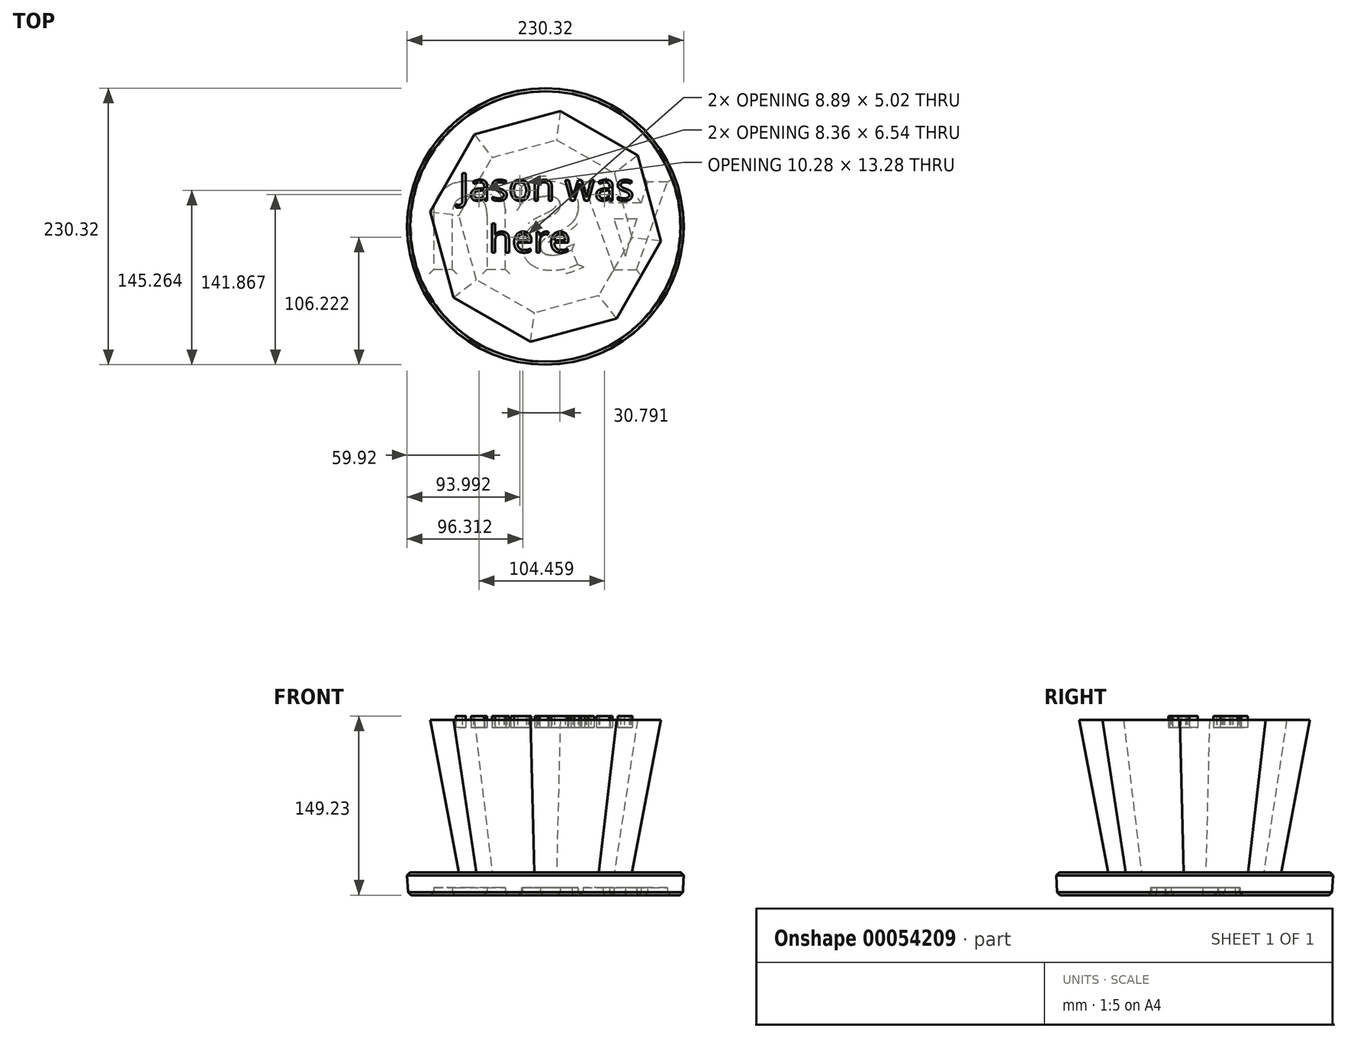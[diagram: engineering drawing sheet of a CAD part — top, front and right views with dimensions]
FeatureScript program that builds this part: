
annotation { "Feature Type Name" : "Feature", "Feature Type Description" : "" }
export const myFeature = defineFeature(function(context is Context, id is Id, definition is map)
    precondition{}
    {
        {
            var Q0;
            Q0=qCreatedBy(makeId("Top.planeOp"),FACE);
            var sketch = newSketch(context, id + "F0", { "sketchPlane" : qUnion([Q0])});
            skCircle(sketch, "E0", {"center": v(3.1, -0.22) * mm, "radius": 114.3 * mm});
            skSolve(sketch);
        }
        {
            var Q0;
            Q0=makeQuery(id+"F0.imprint","IMPRINT",FACE,{"disambiguationData":[TD([[makeQuery(id+"F0.imprint","IMPRINT",EDGE,{"derivedFrom":sQuery(id+"F0.wireOp",EDGE,"E0")}),1.0]])]});
            extrude(context, id + "F1", {"entities" : qUnion([Q0]), "depth" : 19.05 * mm, "hasDraft" : true, "draftAngle" : 3 * degree});
        }
        {
            var Q0;
            Q0=makeQuery(id+"F1.opExtrude","CAP_FACE",FACE,{"disambiguationData":[OSD([sQuery(id+"F0.wireOp",EDGE,"E0")])],"isStart":true});
            var sketch = newSketch(context, id + "F2", { "sketchPlane" : qUnion([Q0])});
            skText(sketch, "E1", { "text": "USA", "fontName": "OpenSans-Bold.ttf"});
            const initialGuessF2  = {"E1": [-0.0985, -0.0367, 1, 0, 0.07327]};
            skSetInitialGuess(sketch, initialGuessF2);
            skSolve(sketch);
        }
        {
            var Q0;
            Q0 = qSketchRegion(id + "F2", true);
            extrude(context, id + "F3", {"entities" : qUnion([Q0]), "operationType" : NewBodyOperationType.REMOVE, "oppositeDirection" : true, "depth" : 6.35 * mm});
        }
        {
            var Q0;
            Q0=makeQuery(id+"F1.opExtrude","CAP_EDGE",EDGE,{"disambiguationData":[OSD([sQuery(id+"F0.wireOp",EDGE,"E0")])],"isStart":true});
            var Q1;
            Q1=makeQuery(id+"F1.opExtrude","CAP_EDGE",EDGE,{"disambiguationData":[OSD([sQuery(id+"F0.wireOp",EDGE,"E0")])],"isStart":false});
            chamfer(context, id + "F4", {"entities" : qUnion([Q0, Q1]), "width" : 2.54 * mm});
        }
        {
            var Q0;
            Q0=makeQuery(id+"F3.boolean.opBoolean","COPY",EDGE,{"derivedFrom":makeQuery(id+"F3.opExtrude","CAP_EDGE",EDGE,{"disambiguationData":[OSD([sQuery(id+"F2.wireOp",EDGE,"E1.sketch_text.stroke-8")])],"isStart":true})});
            var Q1;
            Q1=makeQuery(id+"F3.boolean.opBoolean","COPY",EDGE,{"derivedFrom":makeQuery(id+"F3.opExtrude","CAP_EDGE",EDGE,{"disambiguationData":[OSD([sQuery(id+"F2.wireOp",EDGE,"E1.sketch_text.stroke-9")])],"isStart":true})});
            var Q2;
            Q2=makeQuery(id+"F3.boolean.opBoolean","COPY",EDGE,{"derivedFrom":makeQuery(id+"F3.opExtrude","CAP_EDGE",EDGE,{"disambiguationData":[OSD([sQuery(id+"F2.wireOp",EDGE,"E1.sketch_text.stroke-0")])],"isStart":true})});
            var Q3;
            Q3=makeQuery(id+"F3.boolean.opBoolean","COPY",EDGE,{"derivedFrom":makeQuery(id+"F3.opExtrude","CAP_EDGE",EDGE,{"disambiguationData":[OSD([sQuery(id+"F2.wireOp",EDGE,"E1.sketch_text.stroke-2")])],"isStart":true})});
            var Q4;
            Q4=makeQuery(id+"F3.boolean.opBoolean","COPY",EDGE,{"derivedFrom":makeQuery(id+"F3.opExtrude","CAP_EDGE",EDGE,{"disambiguationData":[OSD([sQuery(id+"F2.wireOp",EDGE,"E1.sketch_text.stroke-1")])],"isStart":true})});
            var Q5;
            Q5=makeQuery(id+"F3.boolean.opBoolean","COPY",EDGE,{"derivedFrom":makeQuery(id+"F3.opExtrude","CAP_EDGE",EDGE,{"disambiguationData":[OSD([sQuery(id+"F2.wireOp",EDGE,"E1.sketch_text.stroke-42")])],"isStart":true})});
            var Q6;
            Q6=makeQuery(id+"F3.boolean.opBoolean","COPY",EDGE,{"derivedFrom":makeQuery(id+"F3.opExtrude","CAP_EDGE",EDGE,{"disambiguationData":[OSD([sQuery(id+"F2.wireOp",EDGE,"E1.sketch_text.stroke-41")])],"isStart":true})});
            var Q7;
            Q7=makeQuery(id+"F3.boolean.opBoolean","COPY",EDGE,{"derivedFrom":makeQuery(id+"F3.opExtrude","CAP_EDGE",EDGE,{"disambiguationData":[OSD([sQuery(id+"F2.wireOp",EDGE,"E1.sketch_text.stroke-37")])],"isStart":true})});
            var Q8;
            Q8=makeQuery(id+"F3.boolean.opBoolean","COPY",EDGE,{"derivedFrom":makeQuery(id+"F3.opExtrude","CAP_EDGE",EDGE,{"disambiguationData":[OSD([sQuery(id+"F2.wireOp",EDGE,"E1.sketch_text.stroke-31")])],"isStart":true})});
            var Q9;
            Q9=makeQuery(id+"F3.boolean.opBoolean","COPY",EDGE,{"derivedFrom":makeQuery(id+"F3.opExtrude","CAP_EDGE",EDGE,{"disambiguationData":[OSD([sQuery(id+"F2.wireOp",EDGE,"E1.sketch_text.stroke-29")])],"isStart":true})});
            var Q10;
            Q10=makeQuery(id+"F3.boolean.opBoolean","COPY",EDGE,{"derivedFrom":makeQuery(id+"F3.opExtrude","CAP_EDGE",EDGE,{"disambiguationData":[OSD([sQuery(id+"F2.wireOp",EDGE,"E1.sketch_text.stroke-26")])],"isStart":true})});
            var Q11;
            Q11=makeQuery(id+"F3.boolean.opBoolean","COPY",EDGE,{"derivedFrom":makeQuery(id+"F3.opExtrude","CAP_EDGE",EDGE,{"disambiguationData":[OSD([sQuery(id+"F2.wireOp",EDGE,"E1.sketch_text.stroke-22")])],"isStart":true})});
            var Q12;
            Q12=makeQuery(id+"F3.boolean.opBoolean","COPY",EDGE,{"derivedFrom":makeQuery(id+"F3.opExtrude","CAP_EDGE",EDGE,{"disambiguationData":[OSD([sQuery(id+"F2.wireOp",EDGE,"E1.sketch_text.stroke-18")])],"isStart":true})});
            var Q13;
            Q13=makeQuery(id+"F3.boolean.opBoolean","COPY",EDGE,{"derivedFrom":makeQuery(id+"F3.opExtrude","CAP_EDGE",EDGE,{"disambiguationData":[OSD([sQuery(id+"F2.wireOp",EDGE,"E1.sketch_text.stroke-20")])],"isStart":true})});
            var Q14;
            Q14=makeQuery(id+"F3.boolean.opBoolean","COPY",EDGE,{"derivedFrom":makeQuery(id+"F3.opExtrude","CAP_EDGE",EDGE,{"disambiguationData":[OSD([sQuery(id+"F2.wireOp",EDGE,"E1.sketch_text.stroke-33")])],"isStart":true})});
            var Q15;
            Q15=makeQuery(id+"F3.boolean.opBoolean","COPY",EDGE,{"derivedFrom":makeQuery(id+"F3.opExtrude","CAP_EDGE",EDGE,{"disambiguationData":[OSD([sQuery(id+"F2.wireOp",EDGE,"E1.sketch_text.stroke-22")])],"isStart":true})});
            var Q16;
            Q16=makeQuery(id+"F3.boolean.opBoolean","COPY",EDGE,{"derivedFrom":makeQuery(id+"F3.opExtrude","CAP_EDGE",EDGE,{"disambiguationData":[OSD([sQuery(id+"F2.wireOp",EDGE,"E1.sketch_text.stroke-47")])],"isStart":true})});
            var Q17;
            Q17=makeQuery(id+"F3.boolean.opBoolean","COPY",EDGE,{"derivedFrom":makeQuery(id+"F3.opExtrude","CAP_EDGE",EDGE,{"disambiguationData":[OSD([sQuery(id+"F2.wireOp",EDGE,"E1.sketch_text.stroke-48")])],"isStart":true})});
            var Q18;
            Q18=makeQuery(id+"F3.boolean.opBoolean","COPY",EDGE,{"derivedFrom":makeQuery(id+"F3.opExtrude","CAP_EDGE",EDGE,{"disambiguationData":[OSD([sQuery(id+"F2.wireOp",EDGE,"E1.sketch_text.stroke-49")])],"isStart":true})});
            var Q19;
            Q19=makeQuery(id+"F3.boolean.opBoolean","COPY",EDGE,{"derivedFrom":makeQuery(id+"F3.opExtrude","CAP_EDGE",EDGE,{"disambiguationData":[OSD([sQuery(id+"F2.wireOp",EDGE,"E1.sketch_text.stroke-53")])],"isStart":true})});
            var Q20;
            Q20=makeQuery(id+"F3.boolean.opBoolean","COPY",EDGE,{"derivedFrom":makeQuery(id+"F3.opExtrude","CAP_EDGE",EDGE,{"disambiguationData":[OSD([sQuery(id+"F2.wireOp",EDGE,"E1.sketch_text.stroke-51")])],"isStart":true})});
            var Q21;
            Q21=makeQuery(id+"F3.boolean.opBoolean","COPY",EDGE,{"derivedFrom":makeQuery(id+"F3.opExtrude","CAP_EDGE",EDGE,{"disambiguationData":[OSD([sQuery(id+"F2.wireOp",EDGE,"E1.sketch_text.stroke-54")])],"isStart":true})});
            var Q22;
            Q22=makeQuery(id+"F3.boolean.opBoolean","COPY",EDGE,{"derivedFrom":makeQuery(id+"F3.opExtrude","CAP_EDGE",EDGE,{"disambiguationData":[OSD([sQuery(id+"F2.wireOp",EDGE,"E1.sketch_text.stroke-44")])],"isStart":true})});
            var Q23;
            Q23=makeQuery(id+"F3.boolean.opBoolean","COPY",EDGE,{"derivedFrom":makeQuery(id+"F3.opExtrude","CAP_EDGE",EDGE,{"disambiguationData":[OSD([sQuery(id+"F2.wireOp",EDGE,"E1.sketch_text.stroke-45")])],"isStart":true})});
            var Q24;
            Q24=makeQuery(id+"F3.boolean.opBoolean","COPY",EDGE,{"derivedFrom":makeQuery(id+"F3.opExtrude","CAP_EDGE",EDGE,{"disambiguationData":[OSD([sQuery(id+"F2.wireOp",EDGE,"E1.sketch_text.stroke-46")])],"isStart":true})});
            var Q25;
            Q25=makeQuery(id+"F3.boolean.opBoolean","COPY",EDGE,{"derivedFrom":makeQuery(id+"F3.opExtrude","CAP_EDGE",EDGE,{"disambiguationData":[OSD([sQuery(id+"F2.wireOp",EDGE,"E1.sketch_text.stroke-43")])],"isStart":true})});
            var Q26;
            Q26=makeQuery(id+"F3.boolean.opBoolean","COPY",EDGE,{"derivedFrom":makeQuery(id+"F3.opExtrude","CAP_EDGE",EDGE,{"disambiguationData":[OSD([sQuery(id+"F2.wireOp",EDGE,"E1.sketch_text.stroke-50")])],"isStart":true})});
            var Q27;
            Q27=makeQuery(id+"F3.boolean.opBoolean","COPY",EDGE,{"derivedFrom":makeQuery(id+"F3.opExtrude","CAP_EDGE",EDGE,{"disambiguationData":[OSD([sQuery(id+"F2.wireOp",EDGE,"E1.sketch_text.stroke-7")])],"isStart":true})});
            var Q28;
            Q28=makeQuery(id+"F3.boolean.opBoolean","COPY",EDGE,{"derivedFrom":makeQuery(id+"F3.opExtrude","CAP_EDGE",EDGE,{"disambiguationData":[OSD([sQuery(id+"F2.wireOp",EDGE,"E1.sketch_text.stroke-14")])],"isStart":true})});
            fillet(context, id + "F5", {"entities" : qUnion([Q0, Q1, Q2, Q3, Q4, Q5, Q6, Q7, Q8, Q9, Q10, Q11, Q12, Q13, Q14, Q15, Q16, Q17, Q18, Q19, Q20, Q21, Q22, Q23, Q24, Q25, Q26, Q27, Q28]), "radius" : 3.8 * mm, "tangentPropagation" : true, "allowEdgeOverflow" : false});
        }
        {
            var Q0;
            Q0=makeQuery(id+"F1.opExtrude","CAP_FACE",FACE,{"disambiguationData":[OSD([sQuery(id+"F0.wireOp",EDGE,"E0")])],"isStart":false});
            var sketch = newSketch(context, id + "F6", { "sketchPlane" : qUnion([Q0])});
            skCircle(sketch, "E2.cCircle", {"center": v(3.1, -0.22) * mm, "radius": 67.1 * mm, "construction": true});
            skLineSegment(sketch, "E2.0", {"start": v(75.13, -9.47) * mm, "end": v(47.49, -57.7) * mm});
            skLineSegment(sketch, "E2.1", {"start": v(47.49, -57.7) * mm, "end": v(-6.16, -72.26) * mm});
            skLineSegment(sketch, "E2.2", {"start": v(-6.16, -72.26) * mm, "end": v(-54.38, -44.62) * mm});
            skLineSegment(sketch, "E2.3", {"start": v(-54.38, -44.62) * mm, "end": v(-68.94, 9.03) * mm});
            skLineSegment(sketch, "E2.4", {"start": v(-68.94, 9.03) * mm, "end": v(-41.3, 57.25) * mm});
            skLineSegment(sketch, "E2.5", {"start": v(-41.3, 57.25) * mm, "end": v(12.34, 71.81) * mm});
            skLineSegment(sketch, "E2.6", {"start": v(12.34, 71.81) * mm, "end": v(60.57, 44.18) * mm});
            skLineSegment(sketch, "E2.7", {"start": v(60.57, 44.18) * mm, "end": v(75.13, -9.47) * mm});
            skPoint(sketch, "E2.0.midPoint", {"position": v(61.3, -33.58) * mm});
            skSolve(sketch);
        }
        {
            var Q0;
            Q0 = qSketchRegion(id + "F6", true);
            extrude(context, id + "F7", {"entities" : qUnion([Q0]), "depth" : 127 * mm, "hasDraft" : true, "draftAngle" : 10 * degree});
        }
        {
            var Q0;
            Q0=makeQuery(id+"F7.opExtrude","CAP_FACE",FACE,{"disambiguationData":[OSD([sQuery(id+"F6.wireOp",EDGE,"E2.0"),sQuery(id+"F6.wireOp",EDGE,"E2.1"),sQuery(id+"F6.wireOp",EDGE,"E2.2"),sQuery(id+"F6.wireOp",EDGE,"E2.3"),sQuery(id+"F6.wireOp",EDGE,"E2.4"),sQuery(id+"F6.wireOp",EDGE,"E2.5"),sQuery(id+"F6.wireOp",EDGE,"E2.6"),sQuery(id+"F6.wireOp",EDGE,"E2.7")])],"isStart":false});
            var sketch = newSketch(context, id + "F8", { "sketchPlane" : qUnion([Q0])});
            skText(sketch, "E3", { "text": "Jason was\n   here", "fontName": "OpenSans-Regular.ttf"});
            skPoint(sketch, "E3.firstSnap0", {"position": v(-74.55, 44.28) * mm});
            const initialGuessF8  = {"E3": [-0.06897, 0.0214, 1, 0, 0.02287]};
            skSetInitialGuess(sketch, initialGuessF8);
            skSolve(sketch);
        }
        {
            var Q0;
            Q0=makeQuery(id+"F8.imprint","IMPRINT",FACE,{"disambiguationData":[TD([[makeQuery(id+"F8.imprint","IMPRINT",EDGE,{"derivedFrom":sQuery(id+"F8.wireOp",EDGE,"E3.sketch_text.stroke-10")}),-1.0]])]});
            var Q1;
            Q1=makeQuery(id+"F8.imprint","IMPRINT",FACE,{"disambiguationData":[TD([[makeQuery(id+"F8.imprint","IMPRINT",EDGE,{"derivedFrom":sQuery(id+"F8.wireOp",EDGE,"E3.sketch_text.stroke-0")}),-1.0]])]});
            var Q2;
            Q2=makeQuery(id+"F8.imprint","IMPRINT",FACE,{"disambiguationData":[TD([[makeQuery(id+"F8.imprint","IMPRINT",EDGE,{"derivedFrom":sQuery(id+"F8.wireOp",EDGE,"E3.sketch_text.stroke-37")}),-1.0]])]});
            var Q3;
            Q3=makeQuery(id+"F8.imprint","IMPRINT",FACE,{"disambiguationData":[TD([[makeQuery(id+"F8.imprint","IMPRINT",EDGE,{"derivedFrom":sQuery(id+"F8.wireOp",EDGE,"E3.sketch_text.stroke-62")}),-1.0]])]});
            var Q4;
            Q4=makeQuery(id+"F8.imprint","IMPRINT",FACE,{"disambiguationData":[TD([[makeQuery(id+"F8.imprint","IMPRINT",EDGE,{"derivedFrom":sQuery(id+"F8.wireOp",EDGE,"E3.sketch_text.stroke-79")}),-1.0]])]});
            var Q5;
            Q5=makeQuery(id+"F8.imprint","IMPRINT",FACE,{"disambiguationData":[TD([[makeQuery(id+"F8.imprint","IMPRINT",EDGE,{"derivedFrom":sQuery(id+"F8.wireOp",EDGE,"E3.sketch_text.stroke-171")}),-1.0]])]});
            var Q6;
            Q6=makeQuery(id+"F8.imprint","IMPRINT",FACE,{"disambiguationData":[TD([[makeQuery(id+"F8.imprint","IMPRINT",EDGE,{"derivedFrom":sQuery(id+"F8.wireOp",EDGE,"E3.sketch_text.stroke-189")}),-1.0]])]});
            var Q7;
            Q7=makeQuery(id+"F8.imprint","IMPRINT",FACE,{"disambiguationData":[TD([[makeQuery(id+"F8.imprint","IMPRINT",EDGE,{"derivedFrom":sQuery(id+"F8.wireOp",EDGE,"E3.sketch_text.stroke-208")}),-1.0]])]});
            var Q8;
            Q8=makeQuery(id+"F8.imprint","IMPRINT",FACE,{"disambiguationData":[TD([[makeQuery(id+"F8.imprint","IMPRINT",EDGE,{"derivedFrom":sQuery(id+"F8.wireOp",EDGE,"E3.sketch_text.stroke-221")}),-1.0]])]});
            var Q9;
            Q9=makeQuery(id+"F8.imprint","IMPRINT",FACE,{"disambiguationData":[TD([[makeQuery(id+"F8.imprint","IMPRINT",EDGE,{"derivedFrom":sQuery(id+"F8.wireOp",EDGE,"E3.sketch_text.stroke-96")}),-1.0]])]});
            var Q10;
            Q10=makeQuery(id+"F8.imprint","IMPRINT",FACE,{"disambiguationData":[TD([[makeQuery(id+"F8.imprint","IMPRINT",EDGE,{"derivedFrom":sQuery(id+"F8.wireOp",EDGE,"E3.sketch_text.stroke-119")}),-1.0]])]});
            var Q11;
            Q11=makeQuery(id+"F8.imprint","IMPRINT",FACE,{"disambiguationData":[TD([[makeQuery(id+"F8.imprint","IMPRINT",EDGE,{"derivedFrom":sQuery(id+"F8.wireOp",EDGE,"E3.sketch_text.stroke-146")}),-1.0]])]});
            extrude(context, id + "F9", {"entities" : qUnion([Q0, Q1, Q2, Q3, Q4, Q5, Q6, Q7, Q8, Q9, Q10, Q11]), "depth" : 3.17 * mm, "hasSecondDirection" : true, "secondDirectionOppositeDirection" : true, "secondDirectionDepth" : 6.35 * mm});
        }
    });
